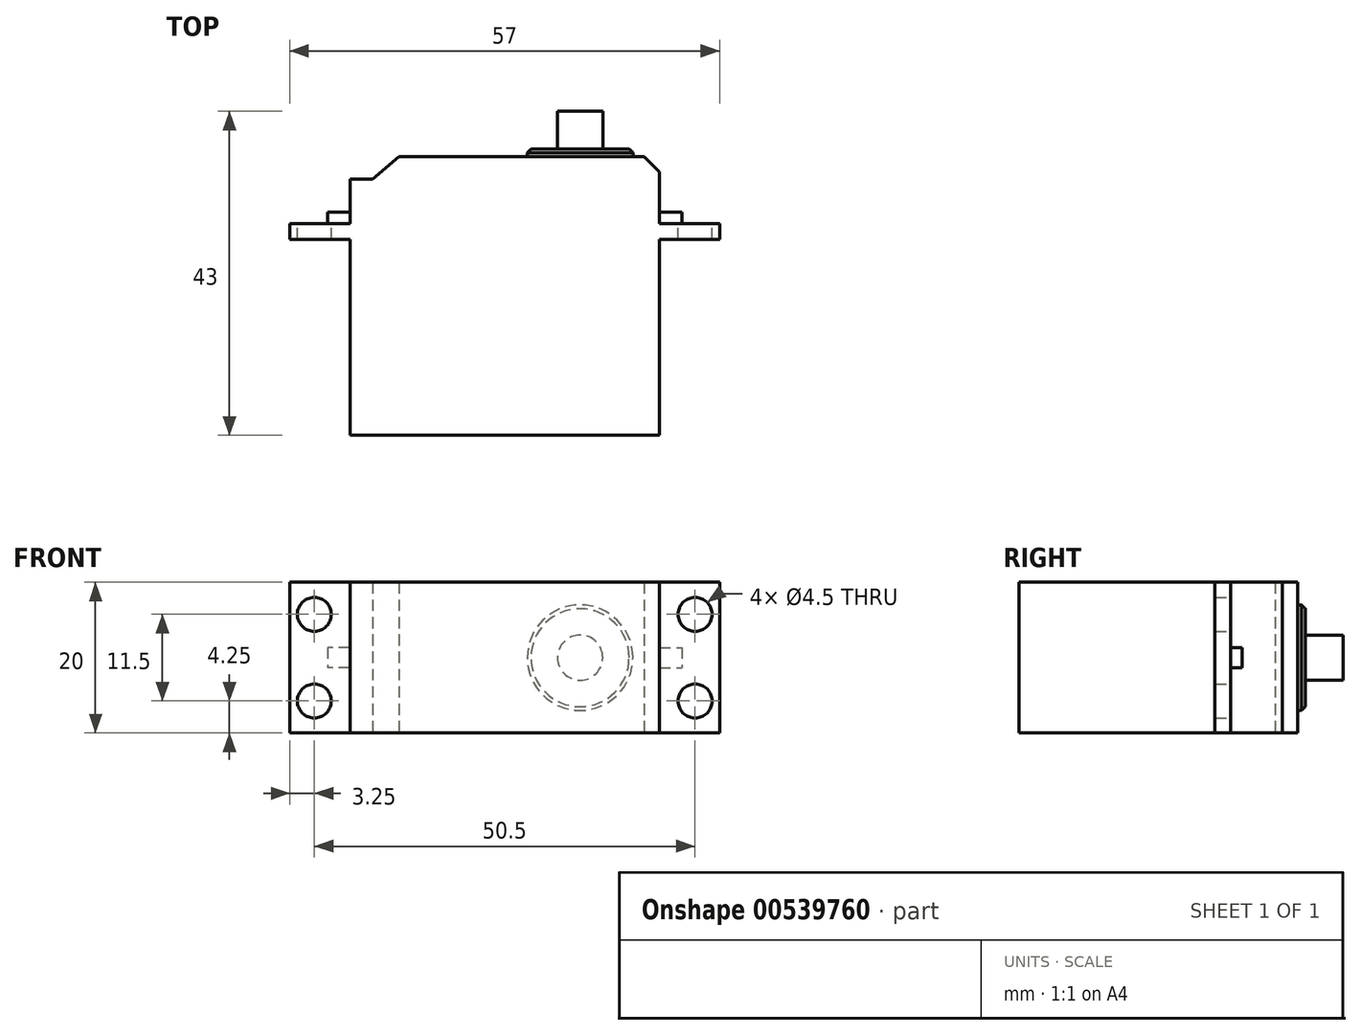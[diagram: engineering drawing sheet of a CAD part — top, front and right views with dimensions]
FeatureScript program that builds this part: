
annotation { "Feature Type Name" : "Feature", "Feature Type Description" : "" }
export const myFeature = defineFeature(function(context is Context, id is Id, definition is map)
    precondition{}
    {
        {
            var Q0;
            Q0=qCreatedBy(makeId("Top.planeOp"),FACE);
            var sketch = newSketch(context, id + "F0", { "sketchPlane" : qUnion([Q0])});
            skLineSegment(sketch, "E0.bottom", {"start": v(20.5, -18.5) * mm, "end": v(-20.5, -18.5) * mm});
            skLineSegment(sketch, "E0.top", {"start": v(18.5, 18.5) * mm, "end": v(-14, 18.5) * mm});
            skLineSegment(sketch, "E0.left", {"start": v(20.5, -18.5) * mm, "end": v(20.5, 16.45) * mm});
            skLineSegment(sketch, "E0.right", {"start": v(-20.5, -18.5) * mm, "end": v(-20.5, 15.5) * mm});
            skPoint(sketch, "E0.middle", {"position": v(0, 0) * mm});
            skLineSegment(sketch, "E1", {"start": v(-14, 18.5) * mm, "end": v(-17.5, 15.5) * mm});
            skLineSegment(sketch, "E2", {"start": v(-17.5, 15.5) * mm, "end": v(-20.5, 15.5) * mm});
            skLineSegment(sketch, "E3", {"start": v(18.5, 18.5) * mm, "end": v(20.5, 16.45) * mm});
            skPoint(sketch, "E4.orphan", {"position": v(-20.5, 18.5) * mm});
            skPoint(sketch, "E5.orphan", {"position": v(20.5, 18.5) * mm});
            skSolve(sketch);
        }
        {
            var Q0;
            Q0=makeQuery(id+"F0.imprint","IMPRINT",FACE,{"disambiguationData":[TD([[makeQuery(id+"F0.imprint","IMPRINT",EDGE,{"derivedFrom":sQuery(id+"F0.wireOp",EDGE,"E0.bottom")}),-1.0]])]});
            extrude(context, id + "F1", {"entities" : qUnion([Q0]), "depth" : 20 * mm, "offsetDistance" : 25 * mm, "symmetric" : true});
        }
        {
            var Q0;
            Q0=makeQuery(id+"F1.opExtrude","SWEPT_FACE",FACE,{"disambiguationData":[OSD([sQuery(id+"F0.wireOp",EDGE,"E0.top")])]});
            var sketch = newSketch(context, id + "F2", { "sketchPlane" : qUnion([Q0])});
            skLineSegment(sketch, "E6.0", {"start": v(-18.5, 10) * mm, "end": v(14, 10) * mm});
            skLineSegment(sketch, "E7.0", {"start": v(-18.5, 10) * mm, "end": v(-18.5, -10) * mm});
            skLineSegment(sketch, "E8.0", {"start": v(-18.5, -10) * mm, "end": v(14, -10) * mm});
            skLineSegment(sketch, "E9.0", {"start": v(14, 10) * mm, "end": v(14, -10) * mm});
            skCircle(sketch, "E10", {"center": v(-10, 0) * mm, "radius": 7 * mm});
            skCircle(sketch, "E11", {"center": v(-10, 0) * mm, "radius": 3 * mm});
            skSolve(sketch);
        }
        {
            var Q0;
            Q0=makeQuery(id+"F2.imprint","IMPRINT",FACE,{"disambiguationData":[TD([[makeQuery(id+"F2.imprint","IMPRINT",EDGE,{"derivedFrom":sQuery(id+"F2.wireOp",EDGE,"E10")}),1.0]])]});
            extrude(context, id + "F3", {"entities" : qUnion([Q0]), "operationType" : NewBodyOperationType.ADD, "depth" : 1 * mm, "offsetDistance" : 25 * mm});
        }
        {
            var Q0;
            Q0=makeQuery(id+"F3.boolean.opBoolean","SPLIT",FACE,{"disambiguationData":[TD([makeQuery(id+"F3.opExtrude","SWEPT_FACE",FACE,{"disambiguationData":[OSD([sQuery(id+"F2.wireOp",EDGE,"E11")])]})])],"derivedFrom":makeQuery(id+"F1.opExtrude","SWEPT_FACE",FACE,{"disambiguationData":[OSD([sQuery(id+"F0.wireOp",EDGE,"E0.top")])]})});
            extrude(context, id + "F4", {"entities" : qUnion([Q0]), "operationType" : NewBodyOperationType.ADD, "depth" : 6 * mm, "offsetDistance" : 25 * mm});
        }
        {
            var Q0;
            Q0=makeQuery(id+"F3.opExtrude","CAP_EDGE",EDGE,{"disambiguationData":[OSD([sQuery(id+"F2.wireOp",EDGE,"E10")])],"isStart":false});
            chamfer(context, id + "F5", {"entities" : qUnion([Q0]), "width" : 0.5 * mm, "tangentPropagation" : true});
        }
        {
            var Q0;
            Q0=makeQuery(id+"F1.opExtrude","SWEPT_FACE",FACE,{"disambiguationData":[OSD([sQuery(id+"F0.wireOp",EDGE,"E0.right")])]});
            var sketch = newSketch(context, id + "F6", { "sketchPlane" : qUnion([Q0])});
            skLineSegment(sketch, "E12.bottom", {"start": v(-9.6, -10) * mm, "end": v(-7.5, -10) * mm});
            skLineSegment(sketch, "E12.top", {"start": v(-9.6, 10) * mm, "end": v(-7.5, 10) * mm});
            skLineSegment(sketch, "E12.left", {"start": v(-9.6, -10) * mm, "end": v(-9.6, 10) * mm});
            skLineSegment(sketch, "E12.right", {"start": v(-7.5, -10) * mm, "end": v(-7.5, 10) * mm});
            skSolve(sketch);
        }
        {
            var Q0;
            Q0=makeQuery(id+"F1.opExtrude","SWEPT_FACE",FACE,{"disambiguationData":[OSD([sQuery(id+"F0.wireOp",EDGE,"E0.left")])]});
            var sketch = newSketch(context, id + "F7", { "sketchPlane" : qUnion([Q0])});
            skLineSegment(sketch, "E13.0", {"start": v(9.6, -10) * mm, "end": v(9.6, 10) * mm});
            skLineSegment(sketch, "E14.1", {"start": v(7.5, -10) * mm, "end": v(7.5, 10) * mm});
            skLineSegment(sketch, "E15.0", {"start": v(9.6, 10) * mm, "end": v(7.5, 10) * mm});
            skLineSegment(sketch, "E16.0", {"start": v(9.6, -10) * mm, "end": v(7.5, -10) * mm});
            skSolve(sketch);
        }
        {
            var Q0;
            Q0=makeQuery(id+"F6.imprint","IMPRINT",FACE,{"disambiguationData":[TD([[makeQuery(id+"F6.imprint","IMPRINT",EDGE,{"derivedFrom":sQuery(id+"F6.wireOp",EDGE,"E12.bottom")}),-1.0]])]});
            extrude(context, id + "F8", {"entities" : qUnion([Q0]), "operationType" : NewBodyOperationType.ADD, "depth" : 8 * mm, "offsetDistance" : 25 * mm});
        }
        {
            var Q0;
            Q0=makeQuery(id+"F7.imprint","IMPRINT",FACE,{"disambiguationData":[TD([[makeQuery(id+"F7.imprint","IMPRINT",EDGE,{"derivedFrom":sQuery(id+"F7.wireOp",EDGE,"E13.0")}),1.0]])]});
            extrude(context, id + "F9", {"entities" : qUnion([Q0]), "operationType" : NewBodyOperationType.ADD, "depth" : 8 * mm, "offsetDistance" : 25 * mm});
        }
        {
            var Q0;
            Q0=makeQuery(id+"F9.opExtrude","SWEPT_FACE",FACE,{"disambiguationData":[OSD([sQuery(id+"F7.wireOp",EDGE,"E13.0")])]});
            var sketch = newSketch(context, id + "F10", { "sketchPlane" : qUnion([Q0])});
            skCircle(sketch, "E17", {"center": v(-25.25, -5.75) * mm, "radius": 2.25 * mm});
            skLineSegment(sketch, "E18", {"start": v(-42, 0) * mm, "end": v(34.94, 0) * mm, "construction": true});
            skPoint(sketch, "E18.endSnap0", {"position": v(-20.5, 0) * mm});
            skLineSegment(sketch, "E19", {"start": v(0, 19.25) * mm, "end": v(0, -13.88) * mm, "construction": true});
            skCircle(sketch, "E20", {"center": v(-25.25, 5.75) * mm, "radius": 2.25 * mm});
            skCircle(sketch, "E21", {"center": v(25.25, 5.75) * mm, "radius": 2.25 * mm});
            skCircle(sketch, "E22", {"center": v(25.25, -5.75) * mm, "radius": 2.25 * mm});
            skLineSegment(sketch, "E23.bottom", {"start": v(-20.5, 1.35) * mm, "end": v(-23.5, 1.35) * mm});
            skLineSegment(sketch, "E23.top", {"start": v(-20.5, -1.35) * mm, "end": v(-23.5, -1.35) * mm});
            skLineSegment(sketch, "E23.left", {"start": v(-20.5, 1.35) * mm, "end": v(-20.5, -1.35) * mm});
            skLineSegment(sketch, "E23.right", {"start": v(-23.5, 1.35) * mm, "end": v(-23.5, -1.35) * mm});
            skLineSegment(sketch, "E24.bottom", {"start": v(20.5, 1.35) * mm, "end": v(23.5, 1.35) * mm});
            skLineSegment(sketch, "E24.top", {"start": v(20.5, -1.35) * mm, "end": v(23.5, -1.35) * mm});
            skLineSegment(sketch, "E24.left", {"start": v(20.5, 1.35) * mm, "end": v(20.5, -1.35) * mm});
            skLineSegment(sketch, "E24.right", {"start": v(23.5, 1.35) * mm, "end": v(23.5, -1.35) * mm});
            skSolve(sketch);
        }
        {
            var Q0;
            Q0=makeQuery(id+"F10.imprint","IMPRINT",FACE,{"disambiguationData":[TD([[makeQuery(id+"F10.imprint","IMPRINT",EDGE,{"derivedFrom":sQuery(id+"F10.wireOp",EDGE,"E20")}),1.0]])]});
            var Q1;
            Q1=makeQuery(id+"F10.imprint","IMPRINT",FACE,{"disambiguationData":[TD([[makeQuery(id+"F10.imprint","IMPRINT",EDGE,{"derivedFrom":sQuery(id+"F10.wireOp",EDGE,"E17")}),1.0]])]});
            var Q2;
            Q2=makeQuery(id+"F10.imprint","IMPRINT",FACE,{"disambiguationData":[TD([[makeQuery(id+"F10.imprint","IMPRINT",EDGE,{"derivedFrom":sQuery(id+"F10.wireOp",EDGE,"E22")}),1.0]])]});
            var Q3;
            Q3=makeQuery(id+"F10.imprint","IMPRINT",FACE,{"disambiguationData":[TD([[makeQuery(id+"F10.imprint","IMPRINT",EDGE,{"derivedFrom":sQuery(id+"F10.wireOp",EDGE,"E21")}),1.0]])]});
            extrude(context, id + "F11", {"entities" : qUnion([Q0, Q1, Q2, Q3]), "operationType" : NewBodyOperationType.REMOVE, "endBound" : BoundingType.THROUGH_ALL, "oppositeDirection" : true, "depth" : 25 * mm, "offsetDistance" : 25 * mm});
        }
        {
            var Q0;
            Q0=makeQuery(id+"F10.imprint","IMPRINT",FACE,{"disambiguationData":[TD([[makeQuery(id+"F10.imprint","IMPRINT",EDGE,{"derivedFrom":sQuery(id+"F10.wireOp",EDGE,"E23.bottom")}),1.0]])]});
            var Q1;
            Q1=makeQuery(id+"F10.imprint","IMPRINT",FACE,{"disambiguationData":[TD([[makeQuery(id+"F10.imprint","IMPRINT",EDGE,{"derivedFrom":sQuery(id+"F10.wireOp",EDGE,"E24.bottom")}),-1.0]])]});
            extrude(context, id + "F12", {"entities" : qUnion([Q0, Q1]), "operationType" : NewBodyOperationType.ADD, "depth" : (4 - 2.5) * mm, "offsetDistance" : 25 * mm});
        }
    });
